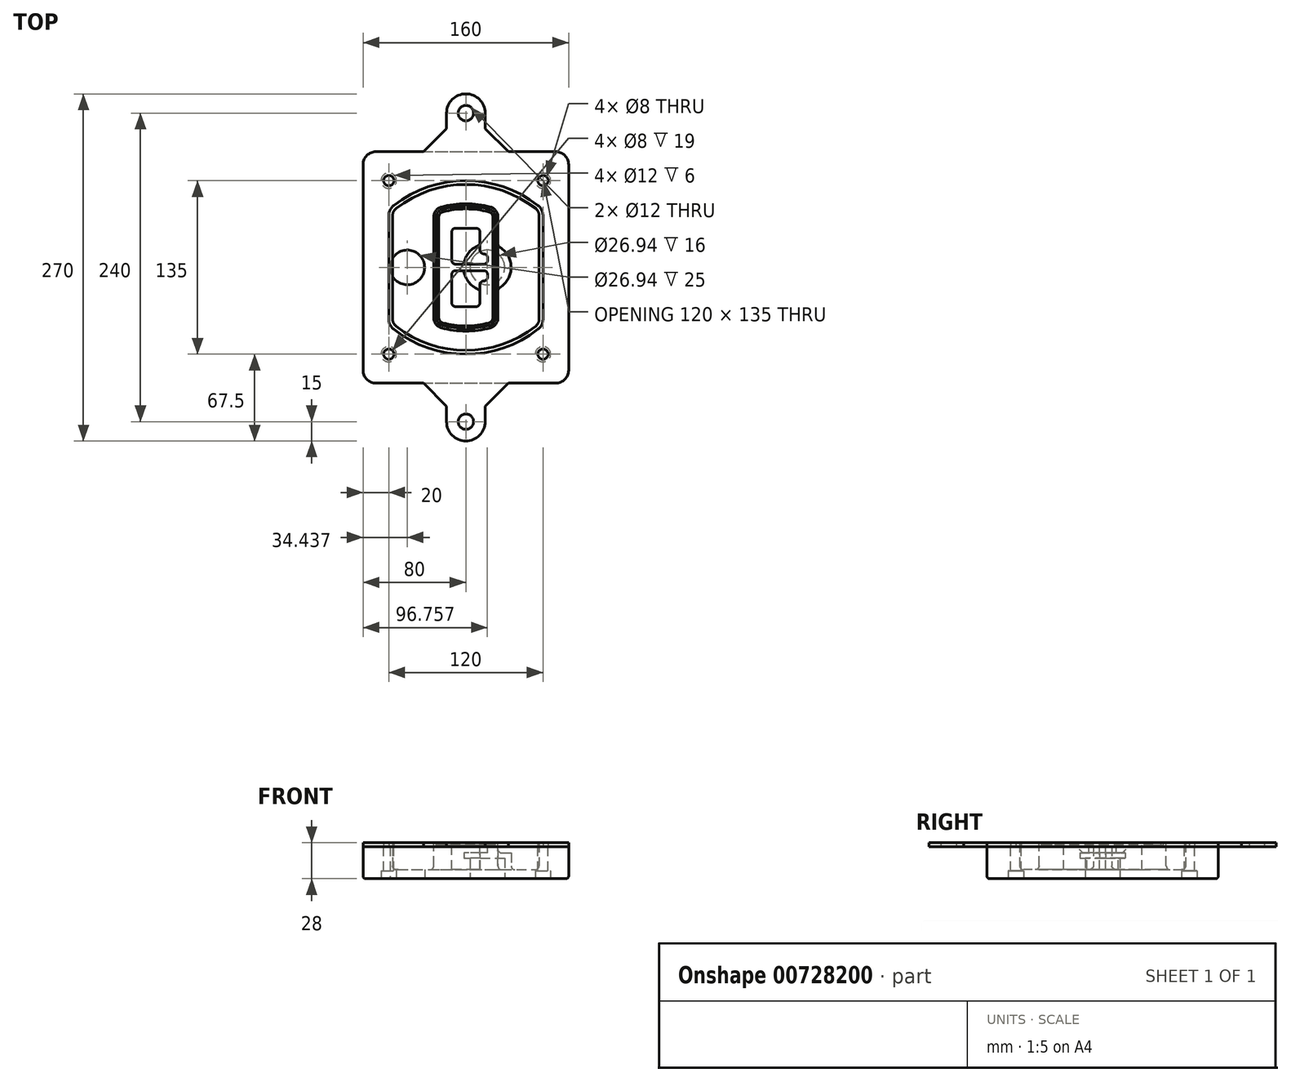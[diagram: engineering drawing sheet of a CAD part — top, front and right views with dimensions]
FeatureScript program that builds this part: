
annotation { "Feature Type Name" : "Feature", "Feature Type Description" : "" }
export const myFeature = defineFeature(function(context is Context, id is Id, definition is map)
    precondition{}
    {
        {
            var Q0;
            Q0=qCreatedBy(makeId("Top.planeOp"),FACE);
            var sketch = newSketch(context, id + "F0", { "sketchPlane" : qUnion([Q0])});
            skPoint(sketch, "E0.rect.middle", {"position": v(0, 0) * mm});
            skLineSegment(sketch, "E1.bottom", {"start": v(-70, -90) * mm, "end": v(70, -90) * mm});
            skLineSegment(sketch, "E1.top", {"start": v(-70, 90) * mm, "end": v(70, 90) * mm});
            skLineSegment(sketch, "E1.left", {"start": v(-80, -80) * mm, "end": v(-80, 80) * mm});
            skLineSegment(sketch, "E1.right", {"start": v(80, -80) * mm, "end": v(80, 80) * mm});
            skLineSegment(sketch, "E2", {"start": v(-80, 90) * mm, "end": v(80, -90) * mm, "construction": true});
            skLineSegment(sketch, "E3", {"start": v(80, 90) * mm, "end": v(-80, -90) * mm, "construction": true});
            skCircle(sketch, "E4", {"center": v(-60, 67.5) * mm, "radius": 4 * mm});
            skCircle(sketch, "E5", {"center": v(60, 67.5) * mm, "radius": 4 * mm});
            skCircle(sketch, "E6", {"center": v(60, -67.5) * mm, "radius": 4 * mm});
            skCircle(sketch, "E7", {"center": v(-60, -67.5) * mm, "radius": 4 * mm});
            skLineSegment(sketch, "E8", {"start": v(-60, 67.5) * mm, "end": v(60, 67.5) * mm, "construction": true});
            skLineSegment(sketch, "E9", {"start": v(60, 67.5) * mm, "end": v(60, -67.5) * mm, "construction": true});
            skLineSegment(sketch, "E10", {"start": v(60, -67.5) * mm, "end": v(-60, -67.5) * mm, "construction": true});
            skLineSegment(sketch, "E11", {"start": v(-60, -67.5) * mm, "end": v(-60, 67.5) * mm, "construction": true});
            skLineSegment(sketch, "E12", {"start": v(-60, 40.3) * mm, "end": v(-60, -40.3) * mm});
            skLineSegment(sketch, "E13", {"start": v(60, 40.3) * mm, "end": v(60, -40.3) * mm});
            skArc(sketch, "E14", {"start": v(56.15, 48.18) * mm, "mid": v(0, 67.5) * mm, "end": v(-56.15, 48.18) * mm});
            skArc(sketch, "E15", {"start": v(-56.15, -48.18) * mm, "mid": v(0, -67.5) * mm, "end": v(56.15, -48.18) * mm});
            skLineSegment(sketch, "E16", {"start": v(-60, 0) * mm, "end": v(60, 0) * mm, "construction": true});
            skPoint(sketch, "E17.visualSharp", {"position": v(-60, -45) * mm});
            skArc(sketch, "E17.filletArc", {"start": v(-60, -40.3) * mm, "mid": v(-58.99, -44.68) * mm, "end": v(-56.15, -48.18) * mm});
            skPoint(sketch, "E18.visualSharp", {"position": v(-60, 45) * mm});
            skArc(sketch, "E18.filletArc", {"start": v(-56.15, 48.18) * mm, "mid": v(-58.99, 44.68) * mm, "end": v(-60, 40.3) * mm});
            skPoint(sketch, "E19.visualSharp", {"position": v(60, 45) * mm});
            skArc(sketch, "E19.filletArc", {"start": v(60, 40.3) * mm, "mid": v(58.99, 44.68) * mm, "end": v(56.15, 48.18) * mm});
            skPoint(sketch, "E20.visualSharp", {"position": v(60, -45) * mm});
            skArc(sketch, "E20.filletArc", {"start": v(56.15, -48.18) * mm, "mid": v(58.99, -44.68) * mm, "end": v(60, -40.3) * mm});
            skPoint(sketch, "E21.visualSharp", {"position": v(-80, 90) * mm});
            skArc(sketch, "E21.filletArc", {"start": v(-70, 90) * mm, "mid": v(-77.07, 87.07) * mm, "end": v(-80, 80) * mm});
            skPoint(sketch, "E22.visualSharp", {"position": v(80, 90) * mm});
            skArc(sketch, "E22.filletArc", {"start": v(80, 80) * mm, "mid": v(77.07, 87.07) * mm, "end": v(70, 90) * mm});
            skPoint(sketch, "E23.visualSharp", {"position": v(80, -90) * mm});
            skArc(sketch, "E23.filletArc", {"start": v(70, -90) * mm, "mid": v(77.07, -87.07) * mm, "end": v(80, -80) * mm});
            skPoint(sketch, "E24.visualSharp", {"position": v(-80, -90) * mm});
            skArc(sketch, "E24.filletArc", {"start": v(-80, -80) * mm, "mid": v(-77.07, -87.07) * mm, "end": v(-70, -90) * mm});
            skArc(sketch, "E25.0", {"start": v(57, 40.3) * mm, "mid": v(56.3, 43.36) * mm, "end": v(54.3, 45.81) * mm});
            skLineSegment(sketch, "E25.1", {"start": v(57, 40.3) * mm, "end": v(57, -40.3) * mm});
            skArc(sketch, "E25.2", {"start": v(54.3, -45.81) * mm, "mid": v(56.3, -43.36) * mm, "end": v(57, -40.3) * mm});
            skArc(sketch, "E25.3", {"start": v(-54.3, -45.81) * mm, "mid": v(0, -64.5) * mm, "end": v(54.3, -45.81) * mm});
            skArc(sketch, "E25.4", {"start": v(-57, -40.3) * mm, "mid": v(-56.3, -43.36) * mm, "end": v(-54.3, -45.81) * mm});
            skArc(sketch, "E25.5", {"start": v(54.3, 45.81) * mm, "mid": v(0, 64.5) * mm, "end": v(-54.3, 45.81) * mm});
            skLineSegment(sketch, "E25.6", {"start": v(-57, 40.3) * mm, "end": v(-57, -40.3) * mm});
            skArc(sketch, "E25.7", {"start": v(-54.3, 45.81) * mm, "mid": v(-56.3, 43.36) * mm, "end": v(-57, 40.3) * mm});
            skArc(sketch, "E26.0", {"start": v(-58.62, 51.33) * mm, "mid": v(-62.58, 46.43) * mm, "end": v(-64, 40.3) * mm});
            skArc(sketch, "E26.1", {"start": v(58.62, 51.33) * mm, "mid": v(0, 71.5) * mm, "end": v(-58.62, 51.33) * mm});
            skArc(sketch, "E26.2", {"start": v(64, 40.3) * mm, "mid": v(62.58, 46.43) * mm, "end": v(58.62, 51.33) * mm});
            skLineSegment(sketch, "E26.3", {"start": v(64, 40.3) * mm, "end": v(64, -40.3) * mm});
            skArc(sketch, "E26.4", {"start": v(58.62, -51.33) * mm, "mid": v(62.58, -46.43) * mm, "end": v(64, -40.3) * mm});
            skLineSegment(sketch, "E26.5", {"start": v(-64, 40.3) * mm, "end": v(-64, -40.3) * mm});
            skArc(sketch, "E26.6", {"start": v(-58.62, -51.33) * mm, "mid": v(0, -71.5) * mm, "end": v(58.62, -51.33) * mm});
            skArc(sketch, "E26.7", {"start": v(-64, -40.3) * mm, "mid": v(-62.58, -46.43) * mm, "end": v(-58.62, -51.33) * mm});
            skSolve(sketch);
        }
        {
            var Q0;
            Q0=makeQuery(id+"F0.imprint","IMPRINT",FACE,{"disambiguationData":[TD([[makeQuery(id+"F0.imprint","IMPRINT",EDGE,{"derivedFrom":sQuery(id+"F0.wireOp",EDGE,"E1.bottom")}),1.0]])]});
            var Q1;
            Q1=makeQuery(id+"F0.imprint","IMPRINT",FACE,{"disambiguationData":[TD([[makeQuery(id+"F0.imprint","IMPRINT",EDGE,{"derivedFrom":sQuery(id+"F0.wireOp",EDGE,"E12")}),1.0]])]});
            var Q2;
            Q2=makeQuery(id+"F0.imprint","IMPRINT",FACE,{"disambiguationData":[TD([[makeQuery(id+"F0.imprint","IMPRINT",EDGE,{"derivedFrom":sQuery(id+"F0.wireOp",EDGE,"E25.0")}),1.0]])]});
            var Q3;
            Q3=makeQuery(id+"F0.imprint","IMPRINT",FACE,{"disambiguationData":[TD([[makeQuery(id+"F0.imprint","IMPRINT",EDGE,{"derivedFrom":sQuery(id+"F0.wireOp",EDGE,"E12")}),-1.0]])]});
            extrude(context, id + "F1", {"entities" : qUnion([Q0, Q1, Q2, Q3]), "oppositeDirection" : true, "depth" : 25 * mm});
        }
        {
            var Q0;
            Q0=makeQuery(id+"F0.imprint","IMPRINT",FACE,{"disambiguationData":[TD([[makeQuery(id+"F0.imprint","IMPRINT",EDGE,{"derivedFrom":sQuery(id+"F0.wireOp",EDGE,"E12")}),1.0]])]});
            extrude(context, id + "F2", {"entities" : qUnion([Q0]), "operationType" : NewBodyOperationType.ADD, "depth" : 3 * mm});
        }
        {
            var Q0;
            Q0=makeQuery(id+"F0.imprint","IMPRINT",FACE,{"disambiguationData":[TD([[makeQuery(id+"F0.imprint","IMPRINT",EDGE,{"derivedFrom":sQuery(id+"F0.wireOp",EDGE,"E25.0")}),1.0]])]});
            extrude(context, id + "F3", {"entities" : qUnion([Q0]), "operationType" : NewBodyOperationType.REMOVE, "oppositeDirection" : true, "depth" : 18 * mm});
        }
        {
            var Q0;
            Q0=makeQuery(id+"F2.opExtrude","CAP_FACE",FACE,{"disambiguationData":[OSD([sQuery(id+"F0.wireOp",EDGE,"E12"),sQuery(id+"F0.wireOp",EDGE,"E13"),sQuery(id+"F0.wireOp",EDGE,"E14"),sQuery(id+"F0.wireOp",EDGE,"E15"),sQuery(id+"F0.wireOp",EDGE,"E17.filletArc"),sQuery(id+"F0.wireOp",EDGE,"E18.filletArc"),sQuery(id+"F0.wireOp",EDGE,"E19.filletArc"),sQuery(id+"F0.wireOp",EDGE,"E20.filletArc"),sQuery(id+"F0.wireOp",EDGE,"E25.0"),sQuery(id+"F0.wireOp",EDGE,"E25.1"),sQuery(id+"F0.wireOp",EDGE,"E25.2"),sQuery(id+"F0.wireOp",EDGE,"E25.3"),sQuery(id+"F0.wireOp",EDGE,"E25.4"),sQuery(id+"F0.wireOp",EDGE,"E25.5"),sQuery(id+"F0.wireOp",EDGE,"E25.6"),sQuery(id+"F0.wireOp",EDGE,"E25.7")])],"isStart":false});
            var sketch = newSketch(context, id + "F4", { "sketchPlane" : qUnion([Q0])});
            skArc(sketch, "E27.0", {"start": v(-19.08, -46.97) * mm, "mid": v(0, -49.5) * mm, "end": v(19.08, -46.97) * mm});
            skArc(sketch, "E28.0", {"start": v(19.08, 46.97) * mm, "mid": v(0, 49.5) * mm, "end": v(-19.08, 46.97) * mm});
            skLineSegment(sketch, "E29", {"start": v(-25, 39.25) * mm, "end": v(-25, -39.25) * mm});
            skLineSegment(sketch, "E30", {"start": v(25, 39.25) * mm, "end": v(25, -39.25) * mm});
            skLineSegment(sketch, "E31", {"start": v(-25, 45.1) * mm, "end": v(25, 45.1) * mm, "construction": true});
            skLineSegment(sketch, "E32", {"start": v(-25, -45.1) * mm, "end": v(25, -45.1) * mm, "construction": true});
            skPoint(sketch, "E33.visualSharp", {"position": v(-25, 45.1) * mm});
            skArc(sketch, "E33.filletArc", {"start": v(-19.08, 46.97) * mm, "mid": v(-23.35, 44.11) * mm, "end": v(-25, 39.25) * mm});
            skPoint(sketch, "E34.visualSharp", {"position": v(25, 45.1) * mm});
            skArc(sketch, "E34.filletArc", {"start": v(25, 39.25) * mm, "mid": v(23.35, 44.11) * mm, "end": v(19.08, 46.97) * mm});
            skPoint(sketch, "E35.visualSharp", {"position": v(25, -45.1) * mm});
            skArc(sketch, "E35.filletArc", {"start": v(19.08, -46.97) * mm, "mid": v(23.35, -44.11) * mm, "end": v(25, -39.25) * mm});
            skPoint(sketch, "E36.visualSharp", {"position": v(-25, -45.1) * mm});
            skArc(sketch, "E36.filletArc", {"start": v(-25, -39.25) * mm, "mid": v(-23.35, -44.11) * mm, "end": v(-19.08, -46.97) * mm});
            skArc(sketch, "E37.0", {"start": v(54.3, 45.81) * mm, "mid": v(0, 64.5) * mm, "end": v(-54.3, 45.81) * mm});
            skArc(sketch, "E37.1", {"start": v(-54.3, 45.81) * mm, "mid": v(-56.3, 43.36) * mm, "end": v(-57, 40.3) * mm});
            skLineSegment(sketch, "E37.2", {"start": v(-57, 40.3) * mm, "end": v(-57, -40.3) * mm});
            skArc(sketch, "E37.3", {"start": v(-57, -40.3) * mm, "mid": v(-56.3, -43.36) * mm, "end": v(-54.3, -45.81) * mm});
            skArc(sketch, "E37.4", {"start": v(-54.3, -45.81) * mm, "mid": v(0, -64.5) * mm, "end": v(54.3, -45.81) * mm});
            skArc(sketch, "E37.5", {"start": v(54.3, -45.81) * mm, "mid": v(56.3, -43.36) * mm, "end": v(57, -40.3) * mm});
            skLineSegment(sketch, "E37.6", {"start": v(57, 40.3) * mm, "end": v(57, -40.3) * mm});
            skArc(sketch, "E37.7", {"start": v(57, 40.3) * mm, "mid": v(56.3, 43.36) * mm, "end": v(54.3, 45.81) * mm});
            skLineSegment(sketch, "E38.0", {"start": v(23, 39.25) * mm, "end": v(23, -39.25) * mm});
            skArc(sketch, "E38.1", {"start": v(18.56, -45.04) * mm, "mid": v(21.76, -42.9) * mm, "end": v(23, -39.25) * mm});
            skArc(sketch, "E38.2", {"start": v(-18.56, -45.04) * mm, "mid": v(0, -47.5) * mm, "end": v(18.56, -45.04) * mm});
            skArc(sketch, "E38.3", {"start": v(-23, -39.25) * mm, "mid": v(-21.76, -42.9) * mm, "end": v(-18.56, -45.04) * mm});
            skLineSegment(sketch, "E38.4", {"start": v(-23, 39.25) * mm, "end": v(-23, -39.25) * mm});
            skArc(sketch, "E38.5", {"start": v(23, 39.25) * mm, "mid": v(21.76, 42.9) * mm, "end": v(18.56, 45.04) * mm});
            skArc(sketch, "E38.6", {"start": v(-18.56, 45.04) * mm, "mid": v(-21.76, 42.9) * mm, "end": v(-23, 39.25) * mm});
            skArc(sketch, "E38.7", {"start": v(18.56, 45.04) * mm, "mid": v(0, 47.5) * mm, "end": v(-18.56, 45.04) * mm});
            skArc(sketch, "E39.0", {"start": v(21, 39.25) * mm, "mid": v(20.18, 41.68) * mm, "end": v(18.04, 43.1) * mm});
            skLineSegment(sketch, "E39.1", {"start": v(21, 39.25) * mm, "end": v(21, -39.25) * mm});
            skArc(sketch, "E39.2", {"start": v(18.04, -43.1) * mm, "mid": v(20.18, -41.68) * mm, "end": v(21, -39.25) * mm});
            skArc(sketch, "E39.3", {"start": v(-18.04, -43.1) * mm, "mid": v(0, -45.5) * mm, "end": v(18.04, -43.1) * mm});
            skArc(sketch, "E39.4", {"start": v(-21, -39.25) * mm, "mid": v(-20.18, -41.68) * mm, "end": v(-18.04, -43.1) * mm});
            skArc(sketch, "E39.5", {"start": v(18.04, 43.1) * mm, "mid": v(0, 45.5) * mm, "end": v(-18.04, 43.1) * mm});
            skLineSegment(sketch, "E39.6", {"start": v(-21, 39.25) * mm, "end": v(-21, -39.25) * mm});
            skArc(sketch, "E39.7", {"start": v(-18.04, 43.1) * mm, "mid": v(-20.18, 41.68) * mm, "end": v(-21, 39.25) * mm});
            skLineSegment(sketch, "E40", {"start": v(-25, 0) * mm, "end": v(25, 0) * mm, "construction": true});
            skLineSegment(sketch, "E41", {"start": v(-11, 5.5) * mm, "end": v(-11, 27.5) * mm});
            skLineSegment(sketch, "E42", {"start": v(-8, 30.5) * mm, "end": v(8, 30.5) * mm});
            skLineSegment(sketch, "E43", {"start": v(11, 27.5) * mm, "end": v(11, 13.5) * mm});
            skLineSegment(sketch, "E44", {"start": v(14, 10.5) * mm, "end": v(14, 10.5) * mm});
            skLineSegment(sketch, "E45", {"start": v(17, 7.5) * mm, "end": v(17, 5.5) * mm});
            skLineSegment(sketch, "E46", {"start": v(14, 2.5) * mm, "end": v(-8, 2.5) * mm});
            skPoint(sketch, "E47.visualSharp", {"position": v(-11, 30.5) * mm});
            skArc(sketch, "E47.filletArc", {"start": v(-8, 30.5) * mm, "mid": v(-10.12, 29.62) * mm, "end": v(-11, 27.5) * mm});
            skPoint(sketch, "E48.visualSharp", {"position": v(11, 30.5) * mm});
            skArc(sketch, "E48.filletArc", {"start": v(11, 27.5) * mm, "mid": v(10.12, 29.62) * mm, "end": v(8, 30.5) * mm});
            skPoint(sketch, "E49.visualSharp", {"position": v(11, 10.5) * mm});
            skArc(sketch, "E49.filletArc", {"start": v(11, 13.5) * mm, "mid": v(11.88, 11.38) * mm, "end": v(14, 10.5) * mm});
            skPoint(sketch, "E50.visualSharp", {"position": v(17, 10.5) * mm});
            skArc(sketch, "E50.filletArc", {"start": v(17, 7.5) * mm, "mid": v(16.12, 9.62) * mm, "end": v(14, 10.5) * mm});
            skPoint(sketch, "E51.visualSharp", {"position": v(17, 2.5) * mm});
            skArc(sketch, "E51.filletArc", {"start": v(14, 2.5) * mm, "mid": v(16.12, 3.38) * mm, "end": v(17, 5.5) * mm});
            skPoint(sketch, "E52.visualSharp", {"position": v(-11, 2.5) * mm});
            skArc(sketch, "E52.filletArc", {"start": v(-11, 5.5) * mm, "mid": v(-10.12, 3.38) * mm, "end": v(-8, 2.5) * mm});
            skLineSegment(sketch, "E53.0.MirrorCS", {"start": v(14, -2.5) * mm, "end": v(-8, -2.5) * mm});
            skArc(sketch, "E54.0.MirrorCS", {"start": v(-11, -5.5) * mm, "mid": v(-10.12, -3.38) * mm, "end": v(-8, -2.5) * mm});
            skLineSegment(sketch, "E55.0.MirrorCS", {"start": v(-11, -5.5) * mm, "end": v(-11, -27.5) * mm});
            skArc(sketch, "E56.0.MirrorCS", {"start": v(-8, -30.5) * mm, "mid": v(-10.12, -29.62) * mm, "end": v(-11, -27.5) * mm});
            skLineSegment(sketch, "E57.0.MirrorCS", {"start": v(-8, -30.5) * mm, "end": v(8, -30.5) * mm});
            skArc(sketch, "E58.0.MirrorCS", {"start": v(11, -27.5) * mm, "mid": v(10.12, -29.62) * mm, "end": v(8, -30.5) * mm});
            skLineSegment(sketch, "E59.0.MirrorCS", {"start": v(11, -27.5) * mm, "end": v(11, -13.5) * mm});
            skArc(sketch, "E60.0.MirrorCS", {"start": v(11, -13.5) * mm, "mid": v(11.88, -11.38) * mm, "end": v(14, -10.5) * mm});
            skArc(sketch, "E61.0.MirrorCS", {"start": v(17, -7.5) * mm, "mid": v(16.12, -9.62) * mm, "end": v(14, -10.5) * mm});
            skLineSegment(sketch, "E62.0.MirrorCS", {"start": v(17, -7.5) * mm, "end": v(17, -5.5) * mm});
            skArc(sketch, "E63.0.MirrorCS", {"start": v(14, -2.5) * mm, "mid": v(16.12, -3.38) * mm, "end": v(17, -5.5) * mm});
            skSolve(sketch);
        }
        {
            var Q0;
            Q0=makeQuery(id+"F4.imprint","IMPRINT",FACE,{"disambiguationData":[TD([[makeQuery(id+"F4.imprint","IMPRINT",EDGE,{"derivedFrom":sQuery(id+"F4.wireOp",EDGE,"E27.0")}),1.0]])]});
            var Q1;
            Q1=makeQuery(id+"F4.imprint","IMPRINT",FACE,{"disambiguationData":[TD([[makeQuery(id+"F4.imprint","IMPRINT",EDGE,{"derivedFrom":sQuery(id+"F4.wireOp",EDGE,"E38.0")}),-1.0]])]});
            var Q2;
            Q2=makeQuery(id+"F4.imprint","IMPRINT",FACE,{"disambiguationData":[TD([[makeQuery(id+"F4.imprint","IMPRINT",EDGE,{"derivedFrom":sQuery(id+"F4.wireOp",EDGE,"E39.0")}),1.0]])]});
            extrude(context, id + "F5", {"entities" : qUnion([Q0, Q1, Q2]), "operationType" : NewBodyOperationType.ADD, "endBound" : BoundingType.UP_TO_NEXT, "oppositeDirection" : true, "depth" : 25 * mm});
        }
        {
            var Q0;
            Q0=makeQuery(id+"F4.imprint","IMPRINT",FACE,{"disambiguationData":[TD([[makeQuery(id+"F4.imprint","IMPRINT",EDGE,{"derivedFrom":sQuery(id+"F4.wireOp",EDGE,"E38.0")}),-1.0]])]});
            extrude(context, id + "F6", {"entities" : qUnion([Q0]), "operationType" : NewBodyOperationType.REMOVE, "oppositeDirection" : true, "depth" : 2 * mm});
        }
        {
            var Q0;
            Q0=makeQuery(id+"F1.opExtrude","CAP_FACE",FACE,{"disambiguationData":[OSD([sQuery(id+"F0.wireOp",EDGE,"E1.bottom"),sQuery(id+"F0.wireOp",EDGE,"E1.top"),sQuery(id+"F0.wireOp",EDGE,"E1.left"),sQuery(id+"F0.wireOp",EDGE,"E1.right"),sQuery(id+"F0.wireOp",EDGE,"E4"),sQuery(id+"F0.wireOp",EDGE,"E5"),sQuery(id+"F0.wireOp",EDGE,"E6"),sQuery(id+"F0.wireOp",EDGE,"E7"),sQuery(id+"F0.wireOp",EDGE,"E21.filletArc"),sQuery(id+"F0.wireOp",EDGE,"E22.filletArc"),sQuery(id+"F0.wireOp",EDGE,"E23.filletArc"),sQuery(id+"F0.wireOp",EDGE,"E24.filletArc")])],"isStart":false});
            var sketch = newSketch(context, id + "F7", { "sketchPlane" : qUnion([Q0])});
            skCircle(sketch, "E64", {"center": v(16.76, 0) * mm, "radius": 13.47 * mm});
            skCircle(sketch, "E65", {"center": v(-45.56, 0) * mm, "radius": 13.47 * mm});
            skLineSegment(sketch, "E66", {"start": v(80, 0) * mm, "end": v(-80, 0) * mm});
            skCircle(sketch, "E67", {"center": v(16.76, 0) * mm, "radius": 18.47 * mm});
            skCircle(sketch, "E68", {"center": v(60, -67.5) * mm, "radius": 6 * mm});
            skCircle(sketch, "E69", {"center": v(-60, -67.5) * mm, "radius": 6 * mm});
            skCircle(sketch, "E70", {"center": v(-60, 67.5) * mm, "radius": 6 * mm});
            skCircle(sketch, "E71", {"center": v(60, 67.5) * mm, "radius": 6 * mm});
            skSolve(sketch);
        }
        {
            var Q0;
            {var subQ1=sQuery(id+"F7.wireOp",EDGE,"E66");var subQ4=sQuery(id+"F7.wireOp",EDGE,"E64");var subQ6=makeQuery(id+"F7.imprint","INTERSECT",VERTEX,{"disambiguationData":[OD(0.0)],"derivedFrom":[subQ4,subQ1]});Q0=makeQuery(id+"F7.imprint","IMPRINT",FACE,{"disambiguationData":[TD([[makeQuery(id+"F7.imprint","IMPRINT",EDGE,{"disambiguationData":[TD([[subQ6,-1.0]])],"derivedFrom":subQ4}),-1.0]])]});}
            var Q1;
            {var subQ0=sQuery(id+"F7.wireOp",EDGE,"E66");var subQ1=sQuery(id+"F7.wireOp",EDGE,"E64");var subQ3=makeQuery(id+"F7.imprint","INTERSECT",VERTEX,{"disambiguationData":[OD(0.0)],"derivedFrom":[subQ1,subQ0]});Q1=makeQuery(id+"F7.imprint","IMPRINT",FACE,{"disambiguationData":[TD([[makeQuery(id+"F7.imprint","IMPRINT",EDGE,{"disambiguationData":[TD([[subQ3,-1.0]])],"derivedFrom":subQ1}),1.0]])]});}
            var Q2;
            {var subQ0=sQuery(id+"F7.wireOp",EDGE,"E66");var subQ1=sQuery(id+"F7.wireOp",EDGE,"E64");var subQ3=makeQuery(id+"F7.imprint","INTERSECT",VERTEX,{"disambiguationData":[OD(0.0)],"derivedFrom":[subQ1,subQ0]});Q2=makeQuery(id+"F7.imprint","IMPRINT",FACE,{"disambiguationData":[TD([[makeQuery(id+"F7.imprint","IMPRINT",EDGE,{"disambiguationData":[TD([[subQ3,1.0]])],"derivedFrom":subQ1}),1.0]])]});}
            var Q3;
            {var subQ1=sQuery(id+"F7.wireOp",EDGE,"E66");var subQ4=sQuery(id+"F7.wireOp",EDGE,"E64");var subQ6=makeQuery(id+"F7.imprint","INTERSECT",VERTEX,{"disambiguationData":[OD(0.0)],"derivedFrom":[subQ4,subQ1]});Q3=makeQuery(id+"F7.imprint","IMPRINT",FACE,{"disambiguationData":[TD([[makeQuery(id+"F7.imprint","IMPRINT",EDGE,{"disambiguationData":[TD([[subQ6,1.0]])],"derivedFrom":subQ4}),-1.0]])]});}
            extrude(context, id + "F8", {"entities" : qUnion([Q0, Q1, Q2, Q3]), "operationType" : NewBodyOperationType.ADD, "oppositeDirection" : true, "depth" : 20 * mm});
        }
        {
            var Q0;
            {var subQ0=sQuery(id+"F7.wireOp",EDGE,"E66");var subQ1=sQuery(id+"F7.wireOp",EDGE,"E64");var subQ3=makeQuery(id+"F7.imprint","INTERSECT",VERTEX,{"disambiguationData":[OD(0.0)],"derivedFrom":[subQ1,subQ0]});Q0=makeQuery(id+"F7.imprint","IMPRINT",FACE,{"disambiguationData":[TD([[makeQuery(id+"F7.imprint","IMPRINT",EDGE,{"disambiguationData":[TD([[subQ3,-1.0]])],"derivedFrom":subQ1}),1.0]])]});}
            var Q1;
            {var subQ0=sQuery(id+"F7.wireOp",EDGE,"E66");var subQ1=sQuery(id+"F7.wireOp",EDGE,"E64");var subQ3=makeQuery(id+"F7.imprint","INTERSECT",VERTEX,{"disambiguationData":[OD(0.0)],"derivedFrom":[subQ1,subQ0]});Q1=makeQuery(id+"F7.imprint","IMPRINT",FACE,{"disambiguationData":[TD([[makeQuery(id+"F7.imprint","IMPRINT",EDGE,{"disambiguationData":[TD([[subQ3,1.0]])],"derivedFrom":subQ1}),1.0]])]});}
            extrude(context, id + "F9", {"entities" : qUnion([Q0, Q1]), "operationType" : NewBodyOperationType.REMOVE, "oppositeDirection" : true, "depth" : 16 * mm});
        }
        {
            var Q0;
            {var subQ0=sQuery(id+"F7.wireOp",EDGE,"E66");var subQ1=sQuery(id+"F7.wireOp",EDGE,"E65");var subQ3=makeQuery(id+"F7.imprint","INTERSECT",VERTEX,{"disambiguationData":[OD(0.0)],"derivedFrom":[subQ1,subQ0]});Q0=makeQuery(id+"F7.imprint","IMPRINT",FACE,{"disambiguationData":[TD([[makeQuery(id+"F7.imprint","IMPRINT",EDGE,{"disambiguationData":[TD([[subQ3,-1.0]])],"derivedFrom":subQ1}),1.0]])]});}
            var Q1;
            {var subQ0=sQuery(id+"F7.wireOp",EDGE,"E66");var subQ1=sQuery(id+"F7.wireOp",EDGE,"E65");var subQ3=makeQuery(id+"F7.imprint","INTERSECT",VERTEX,{"disambiguationData":[OD(0.0)],"derivedFrom":[subQ1,subQ0]});Q1=makeQuery(id+"F7.imprint","IMPRINT",FACE,{"disambiguationData":[TD([[makeQuery(id+"F7.imprint","IMPRINT",EDGE,{"disambiguationData":[TD([[subQ3,1.0]])],"derivedFrom":subQ1}),1.0]])]});}
            extrude(context, id + "F10", {"entities" : qUnion([Q0, Q1]), "operationType" : NewBodyOperationType.REMOVE, "oppositeDirection" : true, "depth" : 25 * mm});
        }
        {
            var Q0;
            Q0=makeQuery(id+"F7.imprint","IMPRINT",FACE,{"disambiguationData":[TD([[makeQuery(id+"F7.imprint","IMPRINT",EDGE,{"derivedFrom":sQuery(id+"F7.wireOp",EDGE,"E68")}),1.0]])]});
            var Q1;
            Q1=makeQuery(id+"F7.imprint","IMPRINT",FACE,{"disambiguationData":[TD([[makeQuery(id+"F7.imprint","IMPRINT",EDGE,{"derivedFrom":makeQuery(id+"F1.opExtrude","CAP_EDGE",EDGE,{"disambiguationData":[OSD([sQuery(id+"F0.wireOp",EDGE,"E5")])],"isStart":false})}),-1.0]])]});
            var Q2;
            Q2=makeQuery(id+"F7.imprint","IMPRINT",FACE,{"disambiguationData":[TD([[makeQuery(id+"F7.imprint","IMPRINT",EDGE,{"derivedFrom":sQuery(id+"F7.wireOp",EDGE,"E69")}),1.0]])]});
            var Q3;
            Q3=makeQuery(id+"F7.imprint","IMPRINT",FACE,{"disambiguationData":[TD([[makeQuery(id+"F7.imprint","IMPRINT",EDGE,{"derivedFrom":makeQuery(id+"F1.opExtrude","CAP_EDGE",EDGE,{"disambiguationData":[OSD([sQuery(id+"F0.wireOp",EDGE,"E4")])],"isStart":false})}),-1.0]])]});
            var Q4;
            Q4=makeQuery(id+"F7.imprint","IMPRINT",FACE,{"disambiguationData":[TD([[makeQuery(id+"F7.imprint","IMPRINT",EDGE,{"derivedFrom":sQuery(id+"F7.wireOp",EDGE,"E70")}),1.0]])]});
            var Q5;
            Q5=makeQuery(id+"F7.imprint","IMPRINT",FACE,{"disambiguationData":[TD([[makeQuery(id+"F7.imprint","IMPRINT",EDGE,{"derivedFrom":makeQuery(id+"F1.opExtrude","CAP_EDGE",EDGE,{"disambiguationData":[OSD([sQuery(id+"F0.wireOp",EDGE,"E7")])],"isStart":false})}),-1.0]])]});
            var Q6;
            Q6=makeQuery(id+"F7.imprint","IMPRINT",FACE,{"disambiguationData":[TD([[makeQuery(id+"F7.imprint","IMPRINT",EDGE,{"derivedFrom":sQuery(id+"F7.wireOp",EDGE,"E71")}),1.0]])]});
            var Q7;
            Q7=makeQuery(id+"F7.imprint","IMPRINT",FACE,{"disambiguationData":[TD([[makeQuery(id+"F7.imprint","IMPRINT",EDGE,{"derivedFrom":makeQuery(id+"F1.opExtrude","CAP_EDGE",EDGE,{"disambiguationData":[OSD([sQuery(id+"F0.wireOp",EDGE,"E6")])],"isStart":false})}),-1.0]])]});
            extrude(context, id + "F11", {"entities" : qUnion([Q0, Q1, Q2, Q3, Q4, Q5, Q6, Q7]), "operationType" : NewBodyOperationType.REMOVE, "oppositeDirection" : true, "depth" : 6 * mm});
        }
        {
            var Q0;
            Q0=makeQuery(id+"F9.boolean.opBoolean","COPY",FACE,{"derivedFrom":makeQuery(id+"F9.opExtrude","CAP_FACE",FACE,{"disambiguationData":[OSD([sQuery(id+"F7.wireOp",EDGE,"E64")])],"isStart":false})});
            var sketch = newSketch(context, id + "F12", { "sketchPlane" : qUnion([Q0])});
            skArc(sketch, "E72.0", {"start": v(11, 17.55) * mm, "mid": v(2.57, 11.82) * mm, "end": v(-1.54, 2.5) * mm});
            skArc(sketch, "E72.1", {"start": v(-1.54, -2.5) * mm, "mid": v(2.57, -11.82) * mm, "end": v(11, -17.55) * mm});
            skLineSegment(sketch, "E73", {"start": v(-1.54, -2.5) * mm, "end": v(14, -2.5) * mm});
            skLineSegment(sketch, "E74.0", {"start": v(14, 2.5) * mm, "end": v(-1.54, 2.5) * mm});
            skArc(sketch, "E74.1", {"start": v(14, 2.5) * mm, "mid": v(16.12, 3.38) * mm, "end": v(17, 5.5) * mm});
            skLineSegment(sketch, "E74.2", {"start": v(17, 7.5) * mm, "end": v(17, 5.5) * mm});
            skArc(sketch, "E74.3", {"start": v(17, 7.5) * mm, "mid": v(16.12, 9.62) * mm, "end": v(14, 10.5) * mm});
            skArc(sketch, "E74.4", {"start": v(11, 13.5) * mm, "mid": v(11.88, 11.38) * mm, "end": v(14, 10.5) * mm});
            skLineSegment(sketch, "E74.5", {"start": v(11, 17.55) * mm, "end": v(11, 13.5) * mm});
            skLineSegment(sketch, "E74.7", {"start": v(14, -2.5) * mm, "end": v(-1.54, -2.5) * mm});
            skArc(sketch, "E74.8", {"start": v(14, -2.5) * mm, "mid": v(16.12, -3.38) * mm, "end": v(17, -5.5) * mm});
            skLineSegment(sketch, "E74.9", {"start": v(17, -7.5) * mm, "end": v(17, -5.5) * mm});
            skArc(sketch, "E74.10", {"start": v(17, -7.5) * mm, "mid": v(16.12, -9.62) * mm, "end": v(14, -10.5) * mm});
            skArc(sketch, "E74.11", {"start": v(11, -13.5) * mm, "mid": v(11.88, -11.38) * mm, "end": v(14, -10.5) * mm});
            skLineSegment(sketch, "E74.12", {"start": v(11, -17.55) * mm, "end": v(11, -13.5) * mm});
            skPoint(sketch, "E75.orphan", {"position": v(11, -27.5) * mm});
            skPoint(sketch, "E76.orphan", {"position": v(-8, -2.5) * mm});
            skPoint(sketch, "E77.orphan", {"position": v(-8, 2.5) * mm});
            skPoint(sketch, "E78.orphan", {"position": v(11, 27.5) * mm});
            skSolve(sketch);
        }
        {
            var Q0;
            {var subQ7=sQuery(id+"F12.wireOp",EDGE,"E72.0");var subQ14=sQuery(id+"F12.wireOp",EDGE,"E72.1");var subQ16=sQuery(id+"F12.wireOp",EDGE,"E74.1");var subQ18=sQuery(id+"F12.wireOp",EDGE,"E74.8");Q0=qUnion([makeQuery(id+"F12.imprint","IMPRINT",FACE,{"disambiguationData":[TD([[makeQuery(id+"F12.imprint","IMPRINT",EDGE,{"derivedFrom":subQ7}),1.0]])]}),makeQuery(id+"F12.imprint","IMPRINT",FACE,{"disambiguationData":[TD([[makeQuery(id+"F12.imprint","IMPRINT",EDGE,{"derivedFrom":subQ14}),1.0]])]}),makeQuery(id+"F12.imprint","IMPRINT",FACE,{"disambiguationData":[TD([[makeQuery(id+"F12.imprint","IMPRINT",EDGE,{"derivedFrom":subQ16}),1.0]])]}),makeQuery(id+"F12.imprint","IMPRINT",FACE,{"disambiguationData":[TD([[makeQuery(id+"F12.imprint","IMPRINT",EDGE,{"derivedFrom":subQ18}),-1.0]])]})]);}
            var Q1;
            Q1=makeQuery(id+"F5.boolean.opBoolean","SPLIT",FACE,{"disambiguationData":[TD([makeQuery(id+"F5.opExtrude","SWEPT_FACE",FACE,{"disambiguationData":[OSD([sQuery(id+"F4.wireOp",EDGE,"E41")])]})])],"derivedFrom":makeQuery(id+"F3.boolean.opBoolean","COPY",FACE,{"derivedFrom":makeQuery(id+"F3.opExtrude","CAP_FACE",FACE,{"disambiguationData":[OSD([sQuery(id+"F0.wireOp",EDGE,"E25.0"),sQuery(id+"F0.wireOp",EDGE,"E25.1"),sQuery(id+"F0.wireOp",EDGE,"E25.2"),sQuery(id+"F0.wireOp",EDGE,"E25.3"),sQuery(id+"F0.wireOp",EDGE,"E25.4"),sQuery(id+"F0.wireOp",EDGE,"E25.5"),sQuery(id+"F0.wireOp",EDGE,"E25.6"),sQuery(id+"F0.wireOp",EDGE,"E25.7")])],"isStart":false})})});
            extrude(context, id + "F13", {"entities" : qUnion([Q0]), "operationType" : NewBodyOperationType.REMOVE, "endBound" : BoundingType.UP_TO_SURFACE, "endBoundEntityFace" : qUnion([Q1]), "depth" : 25 * mm});
        }
        {
            var Q0;
            Q0=makeQuery(id+"F3.boolean.opBoolean","COPY",EDGE,{"derivedFrom":makeQuery(id+"F3.opExtrude","CAP_EDGE",EDGE,{"disambiguationData":[OSD([sQuery(id+"F0.wireOp",EDGE,"E25.6")])],"isStart":false})});
            var Q1;
            Q1=makeQuery(id+"F8.boolean.opBoolean","INTERSECT",EDGE,{"derivedFrom":[makeQuery(id+"F5.opExtrude","SWEPT_FACE",FACE,{"disambiguationData":[OSD([sQuery(id+"F4.wireOp",EDGE,"E30")])]}),makeQuery(id+"F8.opExtrude","CAP_FACE",FACE,{"disambiguationData":[OSD([sQuery(id+"F7.wireOp",EDGE,"E67")])],"isStart":false})]});
            var Q2;
            Q2=makeQuery(id+"F8.boolean.opBoolean","INTERSECT",EDGE,{"disambiguationData":[OD(1.0)],"derivedFrom":[makeQuery(id+"F5.opExtrude","SWEPT_FACE",FACE,{"disambiguationData":[OSD([sQuery(id+"F4.wireOp",EDGE,"E30")])]}),makeQuery(id+"F8.opExtrude","SWEPT_FACE",FACE,{"disambiguationData":[OSD([sQuery(id+"F7.wireOp",EDGE,"E67")])]})]});
            var Q3;
            {var subQ0=sQuery(id+"F4.wireOp",EDGE,"E30");Q3=makeQuery(id+"F8.boolean.opBoolean","SPLIT",EDGE,{"disambiguationData":[TD([makeQuery(id+"F5.opExtrude","SWEPT_FACE",FACE,{"disambiguationData":[OSD([sQuery(id+"F4.wireOp",EDGE,"E35.filletArc")])]})])],"derivedFrom":makeQuery(id+"F5.opExtrude","CAP_EDGE",EDGE,{"disambiguationData":[OSD([subQ0])],"isStart":false})});}
            var Q4;
            {var subQ0=sQuery(id+"F0.wireOp",EDGE,"E25.7");var subQ1=sQuery(id+"F0.wireOp",EDGE,"E25.1");var subQ2=sQuery(id+"F0.wireOp",EDGE,"E25.6");var subQ3=sQuery(id+"F0.wireOp",EDGE,"E25.5");var subQ4=sQuery(id+"F0.wireOp",EDGE,"E25.4");var subQ5=sQuery(id+"F0.wireOp",EDGE,"E25.0");var subQ6=sQuery(id+"F0.wireOp",EDGE,"E25.2");var subQ7=sQuery(id+"F0.wireOp",EDGE,"E25.3");Q4=makeQuery(id+"F8.boolean.opBoolean","INTERSECT",EDGE,{"derivedFrom":[makeQuery(id+"F5.boolean.opBoolean","SPLIT",FACE,{"disambiguationData":[TD([makeQuery(id+"F2.opExtrude","SWEPT_FACE",FACE,{"disambiguationData":[OSD([subQ5])]})])],"derivedFrom":makeQuery(id+"F3.boolean.opBoolean","COPY",FACE,{"derivedFrom":makeQuery(id+"F3.opExtrude","CAP_FACE",FACE,{"disambiguationData":[OSD([subQ5,subQ1,subQ6,subQ7,subQ4,subQ3,subQ2,subQ0])],"isStart":false})})}),makeQuery(id+"F8.opExtrude","SWEPT_FACE",FACE,{"disambiguationData":[OSD([sQuery(id+"F7.wireOp",EDGE,"E67")])]})]});}
            var Q5;
            Q5=makeQuery(id+"F8.boolean.opBoolean","INTERSECT",EDGE,{"disambiguationData":[OD(0.0)],"derivedFrom":[makeQuery(id+"F5.opExtrude","SWEPT_FACE",FACE,{"disambiguationData":[OSD([sQuery(id+"F4.wireOp",EDGE,"E30")])]}),makeQuery(id+"F8.opExtrude","SWEPT_FACE",FACE,{"disambiguationData":[OSD([sQuery(id+"F7.wireOp",EDGE,"E67")])]})]});
            fillet(context, id + "F14", {"entities" : qUnion([Q0, Q1, Q2, Q3, Q4, Q5]), "radius" : 3 * mm, "tangentPropagation" : true, "allowEdgeOverflow" : false});
        }
        {
            var Q0;
            Q0=makeQuery(id+"F1.opExtrude","CAP_EDGE",EDGE,{"disambiguationData":[OSD([sQuery(id+"F0.wireOp",EDGE,"E1.bottom")])],"isStart":false});
            fillet(context, id + "F15", {"entities" : qUnion([Q0]), "radius" : 2 * mm, "tangentPropagation" : true, "allowEdgeOverflow" : false});
        }
        {
            var Q0;
            {var subQ0=sQuery(id+"F0.wireOp",EDGE,"E21.filletArc");var subQ1=sQuery(id+"F0.wireOp",EDGE,"E7");var subQ2=sQuery(id+"F0.wireOp",EDGE,"E6");var subQ3=sQuery(id+"F0.wireOp",EDGE,"E5");var subQ4=sQuery(id+"F0.wireOp",EDGE,"E4");var subQ5=sQuery(id+"F0.wireOp",EDGE,"E22.filletArc");var subQ6=sQuery(id+"F0.wireOp",EDGE,"E1.bottom");var subQ7=sQuery(id+"F0.wireOp",EDGE,"E1.right");var subQ8=sQuery(id+"F0.wireOp",EDGE,"E1.top");var subQ9=sQuery(id+"F0.wireOp",EDGE,"E1.left");var subQ10=sQuery(id+"F0.wireOp",EDGE,"E23.filletArc");var subQ11=sQuery(id+"F0.wireOp",EDGE,"E24.filletArc");Q0=makeQuery(id+"F2.boolean.opBoolean","SPLIT",FACE,{"disambiguationData":[TD([makeQuery(id+"F1.opExtrude","SWEPT_FACE",FACE,{"disambiguationData":[OSD([subQ6])]})])],"derivedFrom":makeQuery(id+"F1.opExtrude","CAP_FACE",FACE,{"disambiguationData":[OSD([subQ6,subQ8,subQ9,subQ7,subQ4,subQ3,subQ2,subQ1,subQ0,subQ5,subQ10,subQ11])],"isStart":true})});}
            var sketch = newSketch(context, id + "F16", { "sketchPlane" : qUnion([Q0])});
            skLineSegment(sketch, "E79.0", {"start": v(-70, 90) * mm, "end": v(70, 90) * mm});
            skArc(sketch, "E79.1", {"start": v(-70, 90) * mm, "mid": v(-77.07, 87.07) * mm, "end": v(-80, 80) * mm});
            skLineSegment(sketch, "E79.2", {"start": v(-80, -80) * mm, "end": v(-80, 80) * mm});
            skLineSegment(sketch, "E79.3", {"start": v(-70, -90) * mm, "end": v(70, -90) * mm});
            skArc(sketch, "E79.4", {"start": v(-80, -80) * mm, "mid": v(-77.07, -87.07) * mm, "end": v(-70, -90) * mm});
            skArc(sketch, "E79.5", {"start": v(70, -90) * mm, "mid": v(77.07, -87.07) * mm, "end": v(80, -80) * mm});
            skLineSegment(sketch, "E79.6", {"start": v(80, -80) * mm, "end": v(80, 80) * mm});
            skArc(sketch, "E79.7", {"start": v(80, 80) * mm, "mid": v(77.07, 87.07) * mm, "end": v(70, 90) * mm});
            skCircle(sketch, "E79.8", {"center": v(60, 67.5) * mm, "radius": 4 * mm});
            skCircle(sketch, "E79.9", {"center": v(60, -67.5) * mm, "radius": 4 * mm});
            skCircle(sketch, "E79.10", {"center": v(-60, -67.5) * mm, "radius": 4 * mm});
            skCircle(sketch, "E79.11", {"center": v(-60, 67.5) * mm, "radius": 4 * mm});
            skArc(sketch, "E79.12", {"start": v(56.15, 48.18) * mm, "mid": v(0, 67.5) * mm, "end": v(-56.15, 48.18) * mm});
            skArc(sketch, "E79.13", {"start": v(-56.15, 48.18) * mm, "mid": v(-58.99, 44.68) * mm, "end": v(-60, 40.3) * mm});
            skLineSegment(sketch, "E79.14", {"start": v(-60, 40.3) * mm, "end": v(-60, -40.3) * mm});
            skArc(sketch, "E79.15", {"start": v(-56.15, -48.18) * mm, "mid": v(0, -67.5) * mm, "end": v(56.15, -48.18) * mm});
            skArc(sketch, "E79.16", {"start": v(-60, -40.3) * mm, "mid": v(-58.99, -44.68) * mm, "end": v(-56.15, -48.18) * mm});
            skArc(sketch, "E79.17", {"start": v(56.15, -48.18) * mm, "mid": v(58.99, -44.68) * mm, "end": v(60, -40.3) * mm});
            skLineSegment(sketch, "E79.18", {"start": v(60, 40.3) * mm, "end": v(60, -40.3) * mm});
            skArc(sketch, "E79.19", {"start": v(60, 40.3) * mm, "mid": v(58.99, 44.68) * mm, "end": v(56.15, 48.18) * mm});
            skLineSegment(sketch, "E80", {"start": v(-33, 90) * mm, "end": v(-15, 108) * mm});
            skLineSegment(sketch, "E81", {"start": v(-15, 108) * mm, "end": v(-15, 120) * mm});
            skLineSegment(sketch, "E82", {"start": v(33, 90) * mm, "end": v(15, 108) * mm});
            skLineSegment(sketch, "E83", {"start": v(15, 108) * mm, "end": v(15, 120) * mm});
            skArc(sketch, "E84", {"start": v(15, 120) * mm, "mid": v(0, 135) * mm, "end": v(-15, 120) * mm});
            skCircle(sketch, "E85", {"center": v(0, 120) * mm, "radius": 6 * mm});
            skLineSegment(sketch, "E86", {"start": v(0, 90) * mm, "end": v(0, 120) * mm, "construction": true});
            skLineSegment(sketch, "E87", {"start": v(-80, 0) * mm, "end": v(80, 0) * mm, "construction": true});
            skLineSegment(sketch, "E88.MirrorCS", {"start": v(-33, -90) * mm, "end": v(-15, -108) * mm});
            skLineSegment(sketch, "E89.MirrorCS", {"start": v(33, -90) * mm, "end": v(15, -108) * mm});
            skLineSegment(sketch, "E90.MirrorCS", {"start": v(15, -108) * mm, "end": v(15, -120) * mm});
            skArc(sketch, "E91.MirrorCS", {"start": v(15, -120) * mm, "mid": v(0, -135) * mm, "end": v(-15, -120) * mm});
            skCircle(sketch, "E92.MirrorC", {"center": v(0, -120) * mm, "radius": 6 * mm});
            skLineSegment(sketch, "E93.MirrorCS", {"start": v(-15, -108) * mm, "end": v(-15, -120) * mm});
            skSolve(sketch);
        }
        {
            var Q0;
            {var subQ0=sQuery(id+"F16.wireOp",EDGE,"E80");Q0=makeQuery(id+"F16.imprint","IMPRINT",FACE,{"disambiguationData":[TD([[makeQuery(id+"F16.imprint","IMPRINT",EDGE,{"derivedFrom":subQ0}),-1.0]])]});}
            var Q1;
            {var subQ1=sQuery(id+"F16.wireOp",EDGE,"E79.1");Q1=makeQuery(id+"F16.imprint","IMPRINT",FACE,{"disambiguationData":[TD([[makeQuery(id+"F16.imprint","IMPRINT",EDGE,{"derivedFrom":subQ1}),1.0]])]});}
            var Q2;
            {var subQ0=sQuery(id+"F16.wireOp",EDGE,"E88.MirrorCS");Q2=makeQuery(id+"F16.imprint","IMPRINT",FACE,{"disambiguationData":[TD([[makeQuery(id+"F16.imprint","IMPRINT",EDGE,{"derivedFrom":subQ0}),1.0]])]});}
            var Q3;
            Q3=makeQuery(id+"F2.opExtrude","CAP_FACE",FACE,{"disambiguationData":[OSD([sQuery(id+"F0.wireOp",EDGE,"E12"),sQuery(id+"F0.wireOp",EDGE,"E13"),sQuery(id+"F0.wireOp",EDGE,"E14"),sQuery(id+"F0.wireOp",EDGE,"E15"),sQuery(id+"F0.wireOp",EDGE,"E17.filletArc"),sQuery(id+"F0.wireOp",EDGE,"E18.filletArc"),sQuery(id+"F0.wireOp",EDGE,"E19.filletArc"),sQuery(id+"F0.wireOp",EDGE,"E20.filletArc"),sQuery(id+"F0.wireOp",EDGE,"E25.0"),sQuery(id+"F0.wireOp",EDGE,"E25.1"),sQuery(id+"F0.wireOp",EDGE,"E25.2"),sQuery(id+"F0.wireOp",EDGE,"E25.3"),sQuery(id+"F0.wireOp",EDGE,"E25.4"),sQuery(id+"F0.wireOp",EDGE,"E25.5"),sQuery(id+"F0.wireOp",EDGE,"E25.6"),sQuery(id+"F0.wireOp",EDGE,"E25.7")])],"isStart":false});
            extrude(context, id + "F17", {"entities" : qUnion([Q0, Q1, Q2]), "endBound" : BoundingType.UP_TO_SURFACE, "depth" : 25 * mm, "endBoundEntityFace" : qUnion([Q3]), "offsetDistance" : 25 * mm});
        }
    });
